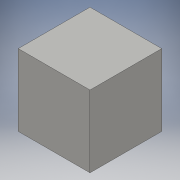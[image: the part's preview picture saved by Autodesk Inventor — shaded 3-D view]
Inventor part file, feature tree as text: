
AUTODESK INVENTOR PART (.ipt)
format: ipt  version: 2016 (Build 200138000, 138)  size: 93,184 bytes
history: native  units: in
note: dims shown in document units (in); Inventor stores cm internally (conversion verified against a paired STEP export)
features: extrude x1, sketch x1
ambient origin geometry x8: Origin, YZ Plane, XZ Plane, XY Plane, X Axis, Y Axis, Z Axis, Center Point
bodies: Body1 (feature_tree)
feature tree (2):
  extrude  "Extrusion2"  Depth=1.9685in
  sketch  "Sketch2"  dims[d4=1.9685in d5=1.9685in d6=1.9685in d7=0.0in]
